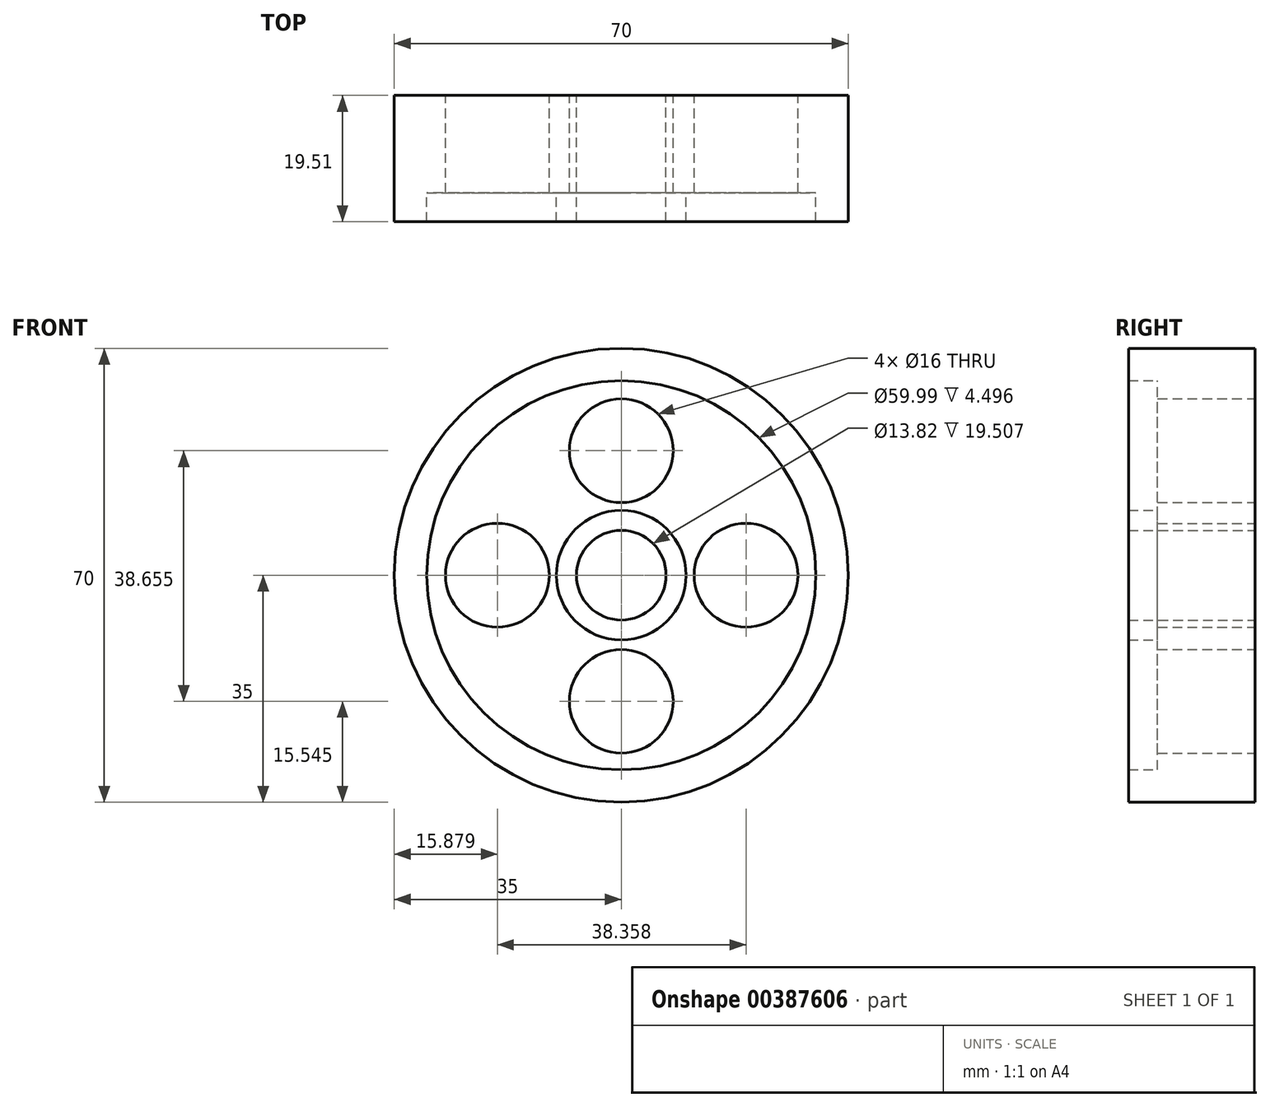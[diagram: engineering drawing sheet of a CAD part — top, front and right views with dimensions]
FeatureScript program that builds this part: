
annotation { "Feature Type Name" : "Feature", "Feature Type Description" : "" }
export const myFeature = defineFeature(function(context is Context, id is Id, definition is map)
    precondition{}
    {
        {
            var Q0;
            Q0=qCreatedBy(makeId("Front.planeOp"),FACE);
            var sketch = newSketch(context, id + "F0", { "sketchPlane" : qUnion([Q0])});
            skCircle(sketch, "E0", {"center": v(0, 0) * mm, "radius": 35 * mm});
            skCircle(sketch, "E1", {"center": v(0, 0) * mm, "radius": 30 * mm});
            skCircle(sketch, "E2", {"center": v(0, 0) * mm, "radius": 10 * mm});
            skCircle(sketch, "E3", {"center": v(0, 0) * mm, "radius": 6.9 * mm});
            skCircle(sketch, "E4", {"center": v(19.24, 0) * mm, "radius": 8 * mm});
            skCircle(sketch, "E5", {"center": v(0, 19.2) * mm, "radius": 8 * mm});
            skCircle(sketch, "E6", {"center": v(-19.12, 0) * mm, "radius": 8 * mm});
            skCircle(sketch, "E7", {"center": v(0, -19.45) * mm, "radius": 8 * mm});
            skSolve(sketch);
        }
        {
            var Q0;
            Q0=makeQuery(id+"F0.imprint","IMPRINT",FACE,{"disambiguationData":[TD([[makeQuery(id+"F0.imprint","IMPRINT",EDGE,{"derivedFrom":sQuery(id+"F0.wireOp",EDGE,"E1")}),1.0]])]});
            var Q1;
            Q1=makeQuery(id+"F0.imprint","IMPRINT",FACE,{"disambiguationData":[TD([[makeQuery(id+"F0.imprint","IMPRINT",EDGE,{"derivedFrom":sQuery(id+"F0.wireOp",EDGE,"E0")}),1.0]])]});
            extrude(context, id + "F1", {"entities" : qUnion([Q0, Q1]), "depth" : 15 * mm});
        }
        {
            var Q0;
            Q0 = qSketchRegion(id + "F0", true);
            var Q1;
            Q1=makeQuery(id+"F0.imprint","IMPRINT",FACE,{"disambiguationData":[TD([[makeQuery(id+"F0.imprint","IMPRINT",EDGE,{"derivedFrom":sQuery(id+"F0.wireOp",EDGE,"E2")}),1.0]])]});
            extrude(context, id + "F2", {"entities" : qUnion([Q0, Q1]), "operationType" : NewBodyOperationType.ADD, "depth" : 19.5 * mm});
        }
    });
